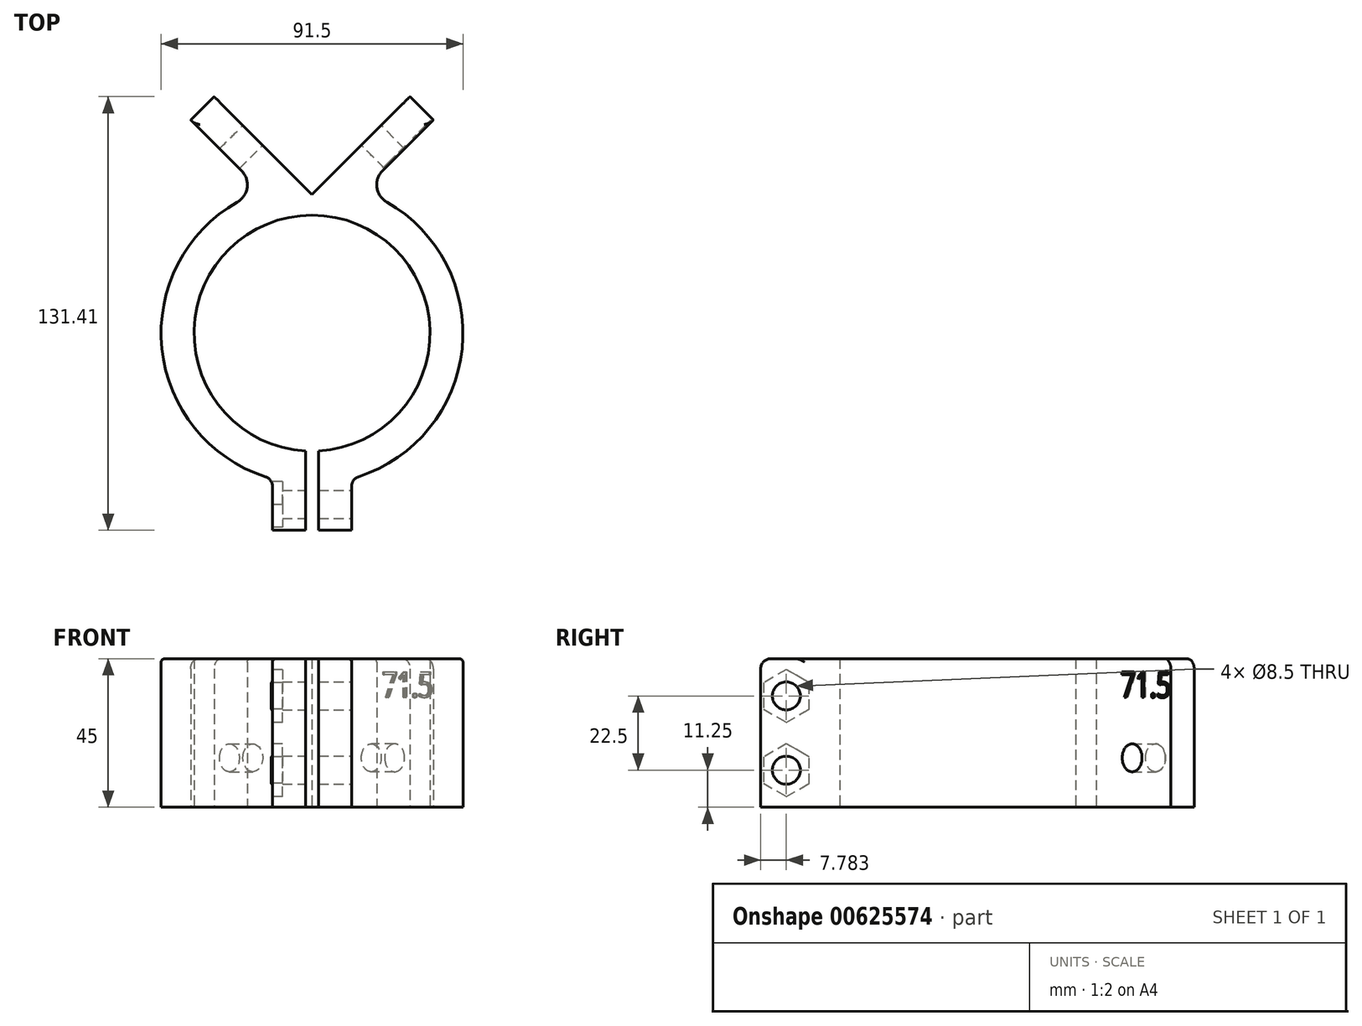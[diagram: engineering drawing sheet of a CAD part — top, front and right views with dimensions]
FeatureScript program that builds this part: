
annotation { "Feature Type Name" : "Feature", "Feature Type Description" : "" }
export const myFeature = defineFeature(function(context is Context, id is Id, definition is map)
    precondition{}
    {
        {
            var Q0;
            Q0=qCreatedBy(makeId("Top.planeOp"),FACE);
            var sketch = newSketch(context, id + "F0", { "sketchPlane" : qUnion([Q0])});
            skLineSegment(sketch, "E0", {"start": v(0, 0) * mm, "end": v(-29.7, 29.7) * mm});
            skLineSegment(sketch, "E1", {"start": v(0, 38.94) * mm, "end": v(0, 0) * mm, "construction": true});
            skLineSegment(sketch, "E2", {"start": v(-29.7, 29.7) * mm, "end": v(-36.77, 22.63) * mm});
            skLineSegment(sketch, "E3", {"start": v(-36.77, 22.63) * mm, "end": v(-15.27, 1.13) * mm});
            skLineSegment(sketch, "E4", {"start": v(0, 0) * mm, "end": v(0, -42) * mm, "construction": true});
            skArc(sketch, "E5", {"start": v(2, -77.7) * mm, "mid": v(0, -6.25) * mm, "end": v(-2, -77.7) * mm});
            skArc(sketch, "E6", {"start": v(2, -87.7) * mm, "mid": v(45.25, -48.76) * mm, "end": v(15.27, 1.13) * mm});
            skLineSegment(sketch, "E7", {"start": v(0, -42) * mm, "end": v(0, -87.75) * mm, "construction": true});
            skLineSegment(sketch, "E8", {"start": v(-2, -87.7) * mm, "end": v(-2, -101.7) * mm});
            skLineSegment(sketch, "E9", {"start": v(-2, -101.7) * mm, "end": v(-12, -101.7) * mm});
            skLineSegment(sketch, "E10", {"start": v(-12, -101.7) * mm, "end": v(-12, -86.15) * mm});
            skLineSegment(sketch, "E11.MirrorCS", {"start": v(2, -101.7) * mm, "end": v(12, -101.7) * mm});
            skLineSegment(sketch, "E12.MirrorCS", {"start": v(12, -101.7) * mm, "end": v(12, -86.15) * mm});
            skLineSegment(sketch, "E13.MirrorCS", {"start": v(2, -87.7) * mm, "end": v(2, -101.7) * mm});
            skLineSegment(sketch, "E14", {"start": v(-2, -87.7) * mm, "end": v(-2, -77.7) * mm});
            skLineSegment(sketch, "E15.MirrorCS", {"start": v(2, -87.7) * mm, "end": v(2, -77.7) * mm});
            skLineSegment(sketch, "E16.MirrorCS", {"start": v(29.7, 29.7) * mm, "end": v(36.77, 22.63) * mm});
            skLineSegment(sketch, "E17.MirrorCS", {"start": v(0, 0) * mm, "end": v(29.7, 29.7) * mm});
            skLineSegment(sketch, "E18.MirrorCS", {"start": v(36.77, 22.63) * mm, "end": v(15.27, 1.13) * mm});
            skPoint(sketch, "E19.orphan", {"position": v(0, -14.14) * mm});
            skArc(sketch, "E20.trimOffspring", {"start": v(-15.27, 1.13) * mm, "mid": v(-45.25, -48.76) * mm, "end": v(-2, -87.7) * mm});
            skLineSegment(sketch, "E21", {"start": v(-9, -76.6) * mm, "end": v(-5.5, -88.7) * mm});
            skLineSegment(sketch, "E22.MirrorCS", {"start": v(9, -76.6) * mm, "end": v(5.5, -88.7) * mm});
            skLineSegment(sketch, "E23", {"start": v(-5.5, -88.7) * mm, "end": v(5.5, -88.7) * mm});
            skSolve(sketch);
        }
        {
            var Q0;
            Q0=makeQuery(id+"F0.imprint","IMPRINT",FACE,{"disambiguationData":[TD([[makeQuery(id+"F0.imprint","IMPRINT",EDGE,{"derivedFrom":sQuery(id+"F0.wireOp",EDGE,"E0")}),1.0]])]});
            var Q1;
            {var subQ4=sQuery(id+"F0.wireOp",EDGE,"E9");Q1=makeQuery(id+"F0.imprint","IMPRINT",FACE,{"disambiguationData":[TD([[makeQuery(id+"F0.imprint","IMPRINT",EDGE,{"derivedFrom":subQ4}),-1.0]])]});}
            var Q2;
            {var subQ1=sQuery(id+"F0.wireOp",EDGE,"E11.MirrorCS");Q2=makeQuery(id+"F0.imprint","IMPRINT",FACE,{"disambiguationData":[TD([[makeQuery(id+"F0.imprint","IMPRINT",EDGE,{"derivedFrom":subQ1}),1.0]])]});}
            var Q3;
            {var subQ0=sQuery(id+"F0.wireOp",EDGE,"E14");Q3=makeQuery(id+"F0.imprint","IMPRINT",FACE,{"disambiguationData":[TD([[makeQuery(id+"F0.imprint","IMPRINT",EDGE,{"derivedFrom":subQ0}),1.0]])]});}
            var Q4;
            {var subQ0=sQuery(id+"F0.wireOp",EDGE,"E15.MirrorCS");Q4=makeQuery(id+"F0.imprint","IMPRINT",FACE,{"disambiguationData":[TD([[makeQuery(id+"F0.imprint","IMPRINT",EDGE,{"derivedFrom":subQ0}),-1.0]])]});}
            var Q5;
            {var subQ3=sQuery(id+"F0.wireOp",EDGE,"E23");var subQ5=sQuery(id+"F0.wireOp",EDGE,"E21");var subQ7=makeQuery(id+"F0.imprint","INTERSECT",VERTEX,{"derivedFrom":[subQ5,subQ3]});Q5=makeQuery(id+"F0.imprint","IMPRINT",FACE,{"disambiguationData":[TD([[makeQuery(id+"F0.imprint","IMPRINT",EDGE,{"disambiguationData":[TD([[subQ7,1.0]])],"derivedFrom":subQ5}),1.0]])]});}
            var Q6;
            {var subQ3=sQuery(id+"F0.wireOp",EDGE,"E22.MirrorCS");var subQ5=sQuery(id+"F0.wireOp",EDGE,"E23");var subQ6=makeQuery(id+"F0.imprint","INTERSECT",VERTEX,{"derivedFrom":[subQ3,subQ5]});Q6=makeQuery(id+"F0.imprint","IMPRINT",FACE,{"disambiguationData":[TD([[makeQuery(id+"F0.imprint","IMPRINT",EDGE,{"disambiguationData":[TD([[subQ6,1.0]])],"derivedFrom":subQ3}),-1.0]])]});}
            extrude(context, id + "F1", {"entities" : qUnion([Q0, Q1, Q2, Q3, Q4, Q5, Q6]), "depth" : 45 * mm, "offsetDistance" : 25 * mm});
        }
        {
            var Q0;
            Q0=makeQuery(id+"F1.opExtrude","SWEPT_FACE",FACE,{"disambiguationData":[OSD([sQuery(id+"F0.wireOp",EDGE,"E17.MirrorCS")])]});
            var sketch = newSketch(context, id + "F2", { "sketchPlane" : qUnion([Q0])});
            skLineSegment(sketch, "E24", {"start": v(0, 15) * mm, "end": v(-50.8, 15) * mm, "construction": true});
            skCircle(sketch, "E25", {"center": v(-25.4, 15) * mm, "radius": 4.25 * mm});
            skSolve(sketch);
        }
        {
            var Q0;
            Q0=qSketchRegion(id+"F2",true);
            extrude(context, id + "F3", {"entities" : qUnion([Q0]), "operationType" : NewBodyOperationType.REMOVE, "endBound" : BoundingType.UP_TO_NEXT, "oppositeDirection" : true, "depth" : 25 * mm, "offsetDistance" : 25 * mm});
        }
        {
            var Q0;
            Q0=makeQuery(id+"F1.opExtrude","SWEPT_FACE",FACE,{"disambiguationData":[OSD([sQuery(id+"F0.wireOp",EDGE,"E0")])]});
            var sketch = newSketch(context, id + "F4", { "sketchPlane" : qUnion([Q0])});
            skLineSegment(sketch, "E26", {"start": v(0, 15) * mm, "end": v(50.8, 15) * mm, "construction": true});
            skCircle(sketch, "E27", {"center": v(25.4, 15) * mm, "radius": 4.25 * mm});
            skSolve(sketch);
        }
        {
            var Q0;
            Q0=qSketchRegion(id+"F4",true);
            extrude(context, id + "F5", {"entities" : qUnion([Q0]), "operationType" : NewBodyOperationType.REMOVE, "endBound" : BoundingType.UP_TO_NEXT, "oppositeDirection" : true, "depth" : 25 * mm, "offsetDistance" : 25 * mm});
        }
        {
            var Q0;
            Q0=makeQuery(id+"F1.opExtrude","SWEPT_FACE",FACE,{"disambiguationData":[OSD([sQuery(id+"F0.wireOp",EDGE,"E12.MirrorCS")])]});
            var sketch = newSketch(context, id + "F6", { "sketchPlane" : qUnion([Q0])});
            skLineSegment(sketch, "E28", {"start": v(-93.93, 45) * mm, "end": v(-93.93, 0) * mm, "construction": true});
            skLineSegment(sketch, "E29", {"start": v(-101.7, 22.5) * mm, "end": v(-86.15, 22.5) * mm, "construction": true});
            skLineSegment(sketch, "E30", {"start": v(-101.7, 22.5) * mm, "end": v(-86.15, 45) * mm, "construction": true});
            skCircle(sketch, "E31", {"center": v(-93.93, 33.75) * mm, "radius": 4.25 * mm});
            skCircle(sketch, "E32.MirrorC", {"center": v(-93.93, 11.25) * mm, "radius": 4.25 * mm});
            skLineSegment(sketch, "E33.MirrorCS", {"start": v(-101.7, 22.5) * mm, "end": v(-86.15, 0) * mm, "construction": true});
            skSolve(sketch);
        }
        {
            var Q0;
            Q0=qSketchRegion(id+"F6",true);
            var Q1;
            Q1=makeQuery(id+"F1.opExtrude","SWEPT_FACE",FACE,{"disambiguationData":[OSD([sQuery(id+"F0.wireOp",EDGE,"E10")])]});
            extrude(context, id + "F7", {"entities" : qUnion([Q0]), "operationType" : NewBodyOperationType.REMOVE, "endBound" : BoundingType.UP_TO_SURFACE, "oppositeDirection" : true, "depth" : 25 * mm, "endBoundEntityFace" : qUnion([Q1]), "offsetDistance" : 25 * mm});
        }
        {
            var Q0;
            Q0=makeQuery(id+"F1.opExtrude","SWEPT_FACE",FACE,{"disambiguationData":[OSD([sQuery(id+"F0.wireOp",EDGE,"E10")])]});
            var sketch = newSketch(context, id + "F8", { "sketchPlane" : qUnion([Q0])});
            skCircle(sketch, "E34.cCircle", {"center": v(93.93, 33.75) * mm, "radius": 6.92 * mm, "construction": true});
            skLineSegment(sketch, "E34.0", {"start": v(93.93, 41.75) * mm, "end": v(100.85, 37.75) * mm});
            skLineSegment(sketch, "E34.1", {"start": v(100.85, 37.75) * mm, "end": v(100.85, 29.75) * mm});
            skLineSegment(sketch, "E34.2", {"start": v(100.85, 29.75) * mm, "end": v(93.93, 25.75) * mm});
            skLineSegment(sketch, "E34.3", {"start": v(93.93, 25.75) * mm, "end": v(87, 29.75) * mm});
            skLineSegment(sketch, "E34.4", {"start": v(87, 29.75) * mm, "end": v(87, 37.75) * mm});
            skLineSegment(sketch, "E34.5", {"start": v(87, 37.75) * mm, "end": v(93.93, 41.75) * mm});
            skPoint(sketch, "E34.0.midPoint", {"position": v(97.39, 39.75) * mm});
            skCircle(sketch, "E35.cCircle", {"center": v(93.93, 11.25) * mm, "radius": 6.92 * mm, "construction": true});
            skLineSegment(sketch, "E35.0", {"start": v(87, 15.25) * mm, "end": v(93.93, 19.25) * mm});
            skLineSegment(sketch, "E35.1", {"start": v(93.93, 19.25) * mm, "end": v(100.85, 15.25) * mm});
            skLineSegment(sketch, "E35.2", {"start": v(100.85, 15.25) * mm, "end": v(100.85, 7.25) * mm});
            skLineSegment(sketch, "E35.3", {"start": v(100.85, 7.25) * mm, "end": v(93.93, 3.25) * mm});
            skLineSegment(sketch, "E35.4", {"start": v(93.93, 3.25) * mm, "end": v(87, 7.25) * mm});
            skLineSegment(sketch, "E35.5", {"start": v(87, 7.25) * mm, "end": v(87, 15.25) * mm});
            skPoint(sketch, "E35.0.midPoint", {"position": v(90.46, 17.25) * mm});
            skSolve(sketch);
        }
        {
            var Q0;
            Q0=qSketchRegion(id+"F8",true);
            extrude(context, id + "F9", {"entities" : qUnion([Q0]), "operationType" : NewBodyOperationType.REMOVE, "oppositeDirection" : true, "depth" : 3 * mm, "offsetDistance" : 25 * mm});
        }
        {
            var Q0;
            Q0=makeQuery(id+"F1.opExtrude","SWEPT_EDGE",EDGE,{"disambiguationData":[OSD([sQuery(id+"F0.wireOp",EDGE,"E3"),sQuery(id+"F0.wireOp",EDGE,"E20.trimOffspring")])]});
            var Q1;
            Q1=makeQuery(id+"F1.opExtrude","SWEPT_EDGE",EDGE,{"disambiguationData":[OSD([sQuery(id+"F0.wireOp",EDGE,"E6"),sQuery(id+"F0.wireOp",EDGE,"E18.MirrorCS")])]});
            fillet(context, id + "F10", {"entities" : qUnion([Q0, Q1]), "radius" : 6 * mm, "tangentPropagation" : true, "allowEdgeOverflow" : false});
        }
        {
            var Q0;
            Q0=makeQuery(id+"F1.opExtrude","CAP_EDGE",EDGE,{"disambiguationData":[OSD([sQuery(id+"F0.wireOp",EDGE,"E9")])],"isStart":false});
            var Q1;
            Q1=makeQuery(id+"F1.opExtrude","CAP_EDGE",EDGE,{"disambiguationData":[OSD([sQuery(id+"F0.wireOp",EDGE,"E11.MirrorCS")])],"isStart":false});
            var Q2;
            Q2=makeQuery(id+"F1.opExtrude","CAP_EDGE",EDGE,{"disambiguationData":[OSD([sQuery(id+"F0.wireOp",EDGE,"E2")])],"isStart":false});
            var Q3;
            Q3=makeQuery(id+"F1.opExtrude","CAP_EDGE",EDGE,{"disambiguationData":[OSD([sQuery(id+"F0.wireOp",EDGE,"E16.MirrorCS")])],"isStart":false});
            var Q4;
            Q4=makeQuery(id+"F1.opExtrude","SWEPT_EDGE",EDGE,{"disambiguationData":[OSD([sQuery(id+"F0.wireOp",EDGE,"E10"),sQuery(id+"F0.wireOp",EDGE,"E20.trimOffspring")])]});
            var Q5;
            Q5=makeQuery(id+"F1.opExtrude","SWEPT_EDGE",EDGE,{"disambiguationData":[OSD([sQuery(id+"F0.wireOp",EDGE,"E6"),sQuery(id+"F0.wireOp",EDGE,"E12.MirrorCS")])]});
            fillet(context, id + "F11", {"entities" : qUnion([Q0, Q1, Q2, Q3, Q4, Q5]), "radius" : 3 * mm, "tangentPropagation" : true, "allowEdgeOverflow" : false});
        }
        {
            var Q0;
            Q0=makeQuery(id+"F1.opExtrude","CAP_EDGE",EDGE,{"disambiguationData":[OSD([sQuery(id+"F0.wireOp",EDGE,"E6")])],"isStart":false});
            var Q1;
            {var subQ0=sQuery(id+"F0.wireOp",EDGE,"E12.MirrorCS");var subQ1=sQuery(id+"F0.wireOp",EDGE,"E6");Q1=makeQuery(id+"F11.opFillet","BLEND_EDGE",EDGE,{"blendedFrom":[makeQuery(id+"F1.opExtrude","SWEPT_EDGE",EDGE,{"disambiguationData":[OSD([subQ1,subQ0])]}),makeQuery(id+"F1.opExtrude","CAP_FACE",FACE,{"disambiguationData":[OSD([sQuery(id+"F0.wireOp",EDGE,"E0"),sQuery(id+"F0.wireOp",EDGE,"E2"),sQuery(id+"F0.wireOp",EDGE,"E3"),sQuery(id+"F0.wireOp",EDGE,"E5"),subQ1,sQuery(id+"F0.wireOp",EDGE,"E8"),sQuery(id+"F0.wireOp",EDGE,"E9"),sQuery(id+"F0.wireOp",EDGE,"E10"),sQuery(id+"F0.wireOp",EDGE,"E11.MirrorCS"),subQ0,sQuery(id+"F0.wireOp",EDGE,"E13.MirrorCS"),sQuery(id+"F0.wireOp",EDGE,"E16.MirrorCS"),sQuery(id+"F0.wireOp",EDGE,"E17.MirrorCS"),sQuery(id+"F0.wireOp",EDGE,"E18.MirrorCS"),sQuery(id+"F0.wireOp",EDGE,"E20.trimOffspring"),sQuery(id+"F0.wireOp",EDGE,"E21"),sQuery(id+"F0.wireOp",EDGE,"E22.MirrorCS"),sQuery(id+"F0.wireOp",EDGE,"E23")])],"isStart":false})],"blendedInto":[makeQuery(id+"F1.opExtrude","CAP_FACE",FACE,{"disambiguationData":[OSD([sQuery(id+"F0.wireOp",EDGE,"E0"),sQuery(id+"F0.wireOp",EDGE,"E2"),sQuery(id+"F0.wireOp",EDGE,"E3"),sQuery(id+"F0.wireOp",EDGE,"E5"),subQ1,sQuery(id+"F0.wireOp",EDGE,"E8"),sQuery(id+"F0.wireOp",EDGE,"E9"),sQuery(id+"F0.wireOp",EDGE,"E10"),sQuery(id+"F0.wireOp",EDGE,"E11.MirrorCS"),subQ0,sQuery(id+"F0.wireOp",EDGE,"E13.MirrorCS"),sQuery(id+"F0.wireOp",EDGE,"E16.MirrorCS"),sQuery(id+"F0.wireOp",EDGE,"E17.MirrorCS"),sQuery(id+"F0.wireOp",EDGE,"E18.MirrorCS"),sQuery(id+"F0.wireOp",EDGE,"E20.trimOffspring"),sQuery(id+"F0.wireOp",EDGE,"E21"),sQuery(id+"F0.wireOp",EDGE,"E22.MirrorCS"),sQuery(id+"F0.wireOp",EDGE,"E23")])],"isStart":false})]});}
            var Q2;
            {var subQ0=sQuery(id+"F0.wireOp",EDGE,"E20.trimOffspring");var subQ1=sQuery(id+"F0.wireOp",EDGE,"E3");Q2=makeQuery(id+"F10.opFillet","BLEND_EDGE",EDGE,{"blendedFrom":[makeQuery(id+"F1.opExtrude","SWEPT_EDGE",EDGE,{"disambiguationData":[OSD([subQ1,subQ0])]}),makeQuery(id+"F1.opExtrude","CAP_FACE",FACE,{"disambiguationData":[OSD([sQuery(id+"F0.wireOp",EDGE,"E0"),sQuery(id+"F0.wireOp",EDGE,"E2"),subQ1,sQuery(id+"F0.wireOp",EDGE,"E5"),sQuery(id+"F0.wireOp",EDGE,"E6"),sQuery(id+"F0.wireOp",EDGE,"E8"),sQuery(id+"F0.wireOp",EDGE,"E9"),sQuery(id+"F0.wireOp",EDGE,"E10"),sQuery(id+"F0.wireOp",EDGE,"E11.MirrorCS"),sQuery(id+"F0.wireOp",EDGE,"E12.MirrorCS"),sQuery(id+"F0.wireOp",EDGE,"E13.MirrorCS"),sQuery(id+"F0.wireOp",EDGE,"E16.MirrorCS"),sQuery(id+"F0.wireOp",EDGE,"E17.MirrorCS"),sQuery(id+"F0.wireOp",EDGE,"E18.MirrorCS"),subQ0,sQuery(id+"F0.wireOp",EDGE,"E21"),sQuery(id+"F0.wireOp",EDGE,"E22.MirrorCS"),sQuery(id+"F0.wireOp",EDGE,"E23")])],"isStart":false})],"blendedInto":[makeQuery(id+"F1.opExtrude","CAP_FACE",FACE,{"disambiguationData":[OSD([sQuery(id+"F0.wireOp",EDGE,"E0"),sQuery(id+"F0.wireOp",EDGE,"E2"),subQ1,sQuery(id+"F0.wireOp",EDGE,"E5"),sQuery(id+"F0.wireOp",EDGE,"E6"),sQuery(id+"F0.wireOp",EDGE,"E8"),sQuery(id+"F0.wireOp",EDGE,"E9"),sQuery(id+"F0.wireOp",EDGE,"E10"),sQuery(id+"F0.wireOp",EDGE,"E11.MirrorCS"),sQuery(id+"F0.wireOp",EDGE,"E12.MirrorCS"),sQuery(id+"F0.wireOp",EDGE,"E13.MirrorCS"),sQuery(id+"F0.wireOp",EDGE,"E16.MirrorCS"),sQuery(id+"F0.wireOp",EDGE,"E17.MirrorCS"),sQuery(id+"F0.wireOp",EDGE,"E18.MirrorCS"),subQ0,sQuery(id+"F0.wireOp",EDGE,"E21"),sQuery(id+"F0.wireOp",EDGE,"E22.MirrorCS"),sQuery(id+"F0.wireOp",EDGE,"E23")])],"isStart":false})]});}
            var Q3;
            Q3=makeQuery(id+"F1.opExtrude","CAP_EDGE",EDGE,{"disambiguationData":[OSD([sQuery(id+"F0.wireOp",EDGE,"E3")])],"isStart":false});
            var Q4;
            Q4=makeQuery(id+"F1.opExtrude","CAP_EDGE",EDGE,{"disambiguationData":[OSD([sQuery(id+"F0.wireOp",EDGE,"E18.MirrorCS")])],"isStart":false});
            var Q5;
            {var subQ0=sQuery(id+"F0.wireOp",EDGE,"E18.MirrorCS");var subQ1=sQuery(id+"F0.wireOp",EDGE,"E6");Q5=makeQuery(id+"F10.opFillet","BLEND_EDGE",EDGE,{"blendedFrom":[makeQuery(id+"F1.opExtrude","SWEPT_EDGE",EDGE,{"disambiguationData":[OSD([subQ1,subQ0])]}),makeQuery(id+"F1.opExtrude","CAP_FACE",FACE,{"disambiguationData":[OSD([sQuery(id+"F0.wireOp",EDGE,"E0"),sQuery(id+"F0.wireOp",EDGE,"E2"),sQuery(id+"F0.wireOp",EDGE,"E3"),sQuery(id+"F0.wireOp",EDGE,"E5"),subQ1,sQuery(id+"F0.wireOp",EDGE,"E8"),sQuery(id+"F0.wireOp",EDGE,"E9"),sQuery(id+"F0.wireOp",EDGE,"E10"),sQuery(id+"F0.wireOp",EDGE,"E11.MirrorCS"),sQuery(id+"F0.wireOp",EDGE,"E12.MirrorCS"),sQuery(id+"F0.wireOp",EDGE,"E13.MirrorCS"),sQuery(id+"F0.wireOp",EDGE,"E16.MirrorCS"),sQuery(id+"F0.wireOp",EDGE,"E17.MirrorCS"),subQ0,sQuery(id+"F0.wireOp",EDGE,"E20.trimOffspring"),sQuery(id+"F0.wireOp",EDGE,"E21"),sQuery(id+"F0.wireOp",EDGE,"E22.MirrorCS"),sQuery(id+"F0.wireOp",EDGE,"E23")])],"isStart":false})],"blendedInto":[makeQuery(id+"F1.opExtrude","CAP_FACE",FACE,{"disambiguationData":[OSD([sQuery(id+"F0.wireOp",EDGE,"E0"),sQuery(id+"F0.wireOp",EDGE,"E2"),sQuery(id+"F0.wireOp",EDGE,"E3"),sQuery(id+"F0.wireOp",EDGE,"E5"),subQ1,sQuery(id+"F0.wireOp",EDGE,"E8"),sQuery(id+"F0.wireOp",EDGE,"E9"),sQuery(id+"F0.wireOp",EDGE,"E10"),sQuery(id+"F0.wireOp",EDGE,"E11.MirrorCS"),sQuery(id+"F0.wireOp",EDGE,"E12.MirrorCS"),sQuery(id+"F0.wireOp",EDGE,"E13.MirrorCS"),sQuery(id+"F0.wireOp",EDGE,"E16.MirrorCS"),sQuery(id+"F0.wireOp",EDGE,"E17.MirrorCS"),subQ0,sQuery(id+"F0.wireOp",EDGE,"E20.trimOffspring"),sQuery(id+"F0.wireOp",EDGE,"E21"),sQuery(id+"F0.wireOp",EDGE,"E22.MirrorCS"),sQuery(id+"F0.wireOp",EDGE,"E23")])],"isStart":false})]});}
            var Q6;
            {var subQ0=sQuery(id+"F0.wireOp",EDGE,"E20.trimOffspring");var subQ1=sQuery(id+"F0.wireOp",EDGE,"E10");Q6=makeQuery(id+"F11.opFillet","BLEND_EDGE",EDGE,{"blendedFrom":[makeQuery(id+"F1.opExtrude","SWEPT_EDGE",EDGE,{"disambiguationData":[OSD([subQ1,subQ0])]}),makeQuery(id+"F1.opExtrude","CAP_FACE",FACE,{"disambiguationData":[OSD([sQuery(id+"F0.wireOp",EDGE,"E0"),sQuery(id+"F0.wireOp",EDGE,"E2"),sQuery(id+"F0.wireOp",EDGE,"E3"),sQuery(id+"F0.wireOp",EDGE,"E5"),sQuery(id+"F0.wireOp",EDGE,"E6"),sQuery(id+"F0.wireOp",EDGE,"E8"),sQuery(id+"F0.wireOp",EDGE,"E9"),subQ1,sQuery(id+"F0.wireOp",EDGE,"E11.MirrorCS"),sQuery(id+"F0.wireOp",EDGE,"E12.MirrorCS"),sQuery(id+"F0.wireOp",EDGE,"E13.MirrorCS"),sQuery(id+"F0.wireOp",EDGE,"E16.MirrorCS"),sQuery(id+"F0.wireOp",EDGE,"E17.MirrorCS"),sQuery(id+"F0.wireOp",EDGE,"E18.MirrorCS"),subQ0,sQuery(id+"F0.wireOp",EDGE,"E21"),sQuery(id+"F0.wireOp",EDGE,"E22.MirrorCS"),sQuery(id+"F0.wireOp",EDGE,"E23")])],"isStart":false})],"blendedInto":[makeQuery(id+"F1.opExtrude","CAP_FACE",FACE,{"disambiguationData":[OSD([sQuery(id+"F0.wireOp",EDGE,"E0"),sQuery(id+"F0.wireOp",EDGE,"E2"),sQuery(id+"F0.wireOp",EDGE,"E3"),sQuery(id+"F0.wireOp",EDGE,"E5"),sQuery(id+"F0.wireOp",EDGE,"E6"),sQuery(id+"F0.wireOp",EDGE,"E8"),sQuery(id+"F0.wireOp",EDGE,"E9"),subQ1,sQuery(id+"F0.wireOp",EDGE,"E11.MirrorCS"),sQuery(id+"F0.wireOp",EDGE,"E12.MirrorCS"),sQuery(id+"F0.wireOp",EDGE,"E13.MirrorCS"),sQuery(id+"F0.wireOp",EDGE,"E16.MirrorCS"),sQuery(id+"F0.wireOp",EDGE,"E17.MirrorCS"),sQuery(id+"F0.wireOp",EDGE,"E18.MirrorCS"),subQ0,sQuery(id+"F0.wireOp",EDGE,"E21"),sQuery(id+"F0.wireOp",EDGE,"E22.MirrorCS"),sQuery(id+"F0.wireOp",EDGE,"E23")])],"isStart":false})]});}
            var Q7;
            Q7=makeQuery(id+"F1.opExtrude","CAP_EDGE",EDGE,{"disambiguationData":[OSD([sQuery(id+"F0.wireOp",EDGE,"E20.trimOffspring")])],"isStart":false});
            fillet(context, id + "F12", {"entities" : qUnion([Q0, Q1, Q2, Q3, Q4, Q5, Q6, Q7]), "radius" : 1 * mm, "allowEdgeOverflow" : false});
        }
        {
            var Q0;
            Q0=makeQuery(id+"F1.opExtrude","SWEPT_FACE",FACE,{"disambiguationData":[OSD([sQuery(id+"F0.wireOp",EDGE,"E18.MirrorCS")])]});
            var sketch = newSketch(context, id + "F13", { "sketchPlane" : qUnion([Q0])});
            skText(sketch, "E36", { "text": "71.5\n", "fontName": "OpenSans-Regular.ttf"});
            const initialGuessF13  = {"E36": [0.02052, 0.0333, 1, 0, 0.00778]};
            skSetInitialGuess(sketch, initialGuessF13);
            skSolve(sketch);
        }
        {
            var Q0;
            Q0 = qSketchRegion(id + "F13", true);
            extrude(context, id + "F14", {"entities" : qUnion([Q0]), "operationType" : NewBodyOperationType.REMOVE, "oppositeDirection" : true, "depth" : 0.5 * mm, "offsetDistance" : 25 * mm});
        }
    });
